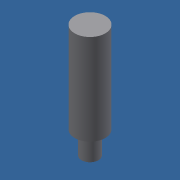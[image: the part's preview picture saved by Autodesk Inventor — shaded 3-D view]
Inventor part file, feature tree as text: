
AUTODESK INVENTOR PART (.ipt)
format: ipt  version: 2018 (Build 220112000, 112)  size: 80,896 bytes
history: native  units: mm
features: other x3, extrude x2, sketch x2, reference x1
ambient origin geometry x8: Origin, YZ Plane, XZ Plane, XY Plane, X Axis, Y Axis, Z Axis, Center Point
bodies: Solid1 (feature_tree)
feature tree (8):
  extrude  "Extrusion1"  Depth=80.0mm TaperAngle=0.0deg
  extrude  "Extrusion2"  [1 undecoded]
  sketch  "Sketch1"  dims[d0=20.0mm d1=0.0mm d2=80.0mm d3=0.0mm]
  reference  "Reference1"
  sketch  "Sketch2"
  other  "<userpath>\OneDrive\Objet3D\EPFLEplucheCarrote\Assembly1.iam"
  other  "Assembly1.iam"
  other  "Manivelle:1"
note: 1 required parameter value undecoded (feature->parameter linkage not recoverable at this tier; creation-order binding heuristic only, values carry confidence <= 0.55)
